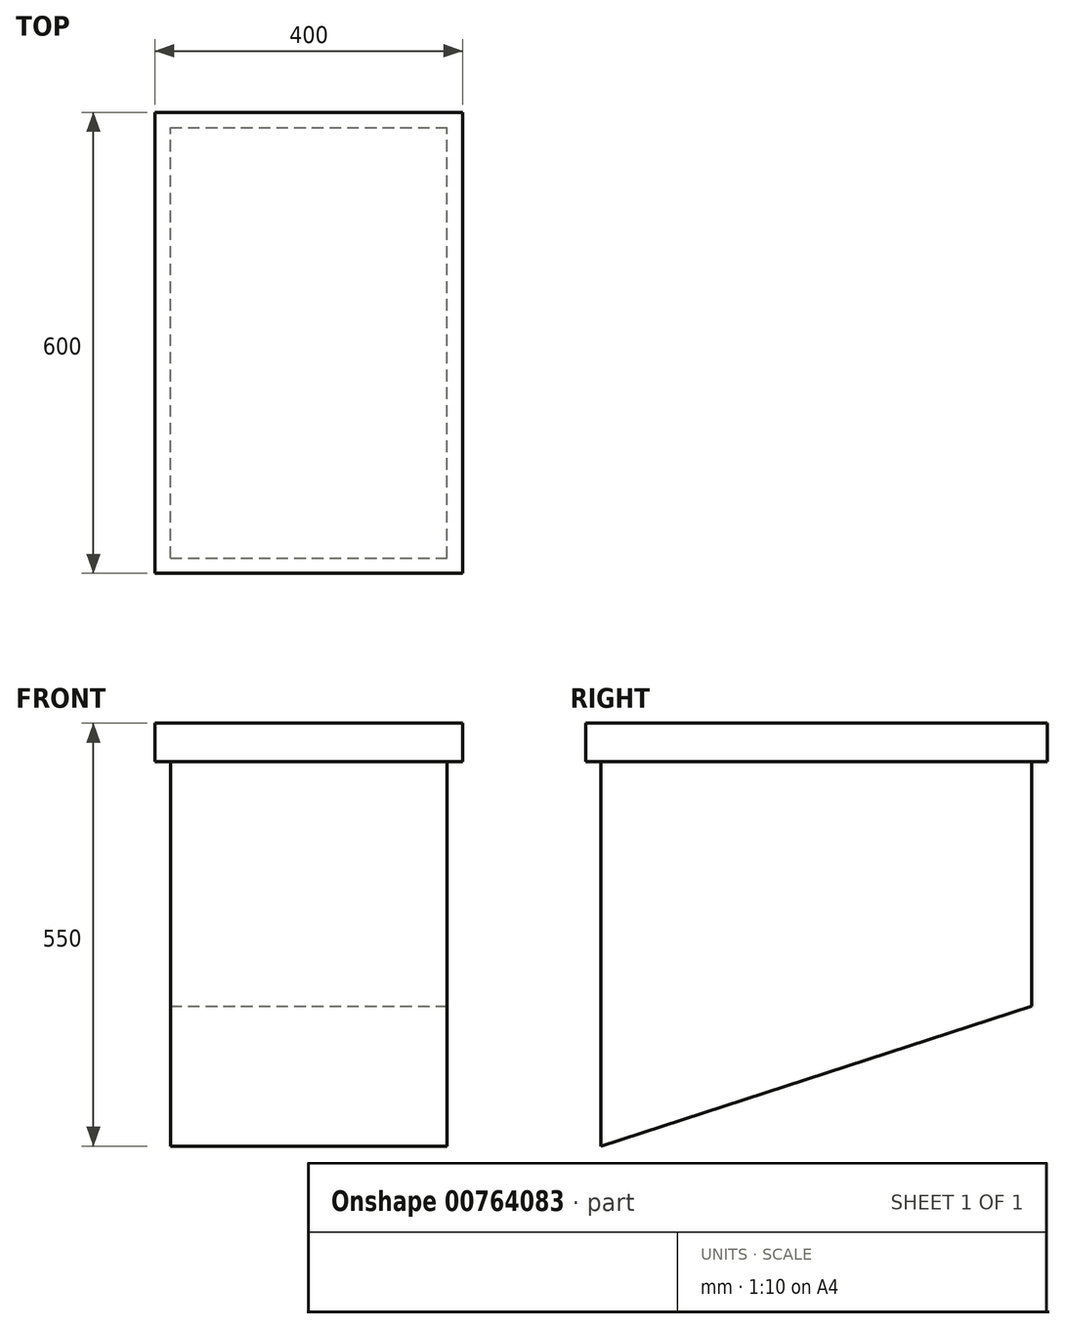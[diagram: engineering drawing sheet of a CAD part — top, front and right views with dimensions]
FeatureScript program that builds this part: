
annotation { "Feature Type Name" : "Feature", "Feature Type Description" : "" }
export const myFeature = defineFeature(function(context is Context, id is Id, definition is map)
    precondition{}
    {
        {
            var Q0;
            Q0=qCreatedBy(makeId("Top.planeOp"),FACE);
            var sketch = newSketch(context, id + "F0", { "sketchPlane" : qUnion([Q0])});
            skLineSegment(sketch, "E0.bottom", {"start": v(-180, 280) * mm, "end": v(180, 280) * mm});
            skLineSegment(sketch, "E0.top", {"start": v(-180, -280) * mm, "end": v(180, -280) * mm});
            skLineSegment(sketch, "E0.left", {"start": v(-180, 280) * mm, "end": v(-180, -280) * mm});
            skLineSegment(sketch, "E0.right", {"start": v(180, 280) * mm, "end": v(180, -280) * mm});
            skPoint(sketch, "E0.middle", {"position": v(0, 0) * mm});
            skSolve(sketch);
        }
        {
            var Q0;
            Q0 = qSketchRegion(id + "F0", true);
            var sketch = newSketch(context, id + "F1", { "sketchPlane" : qUnion([Q0])});
            skSolve(sketch);
        }
        {
            var Q0;
            Q0 = qSketchRegion(id + "F0", true);
            var Q1;
            Q1=makeQuery(id+"F1.imprint","IMPRINT",FACE,{"disambiguationData":[TD([[makeQuery(id+"F1.imprint","IMPRINT",EDGE,{"derivedFrom":makeQuery(id+"F0.imprint","IMPRINT",EDGE,{"derivedFrom":sQuery(id+"F0.wireOp",EDGE,"E0.bottom")})}),-1.0]])]});
            extrude(context, id + "F2", {"entities" : qUnion([Q0, Q1]), "depth" : 500 * mm, "offsetDistance" : 25 * mm});
        }
        {
            var Q0;
            {var subQ0=sQuery(id+"F0.wireOp",EDGE,"E0.right");var subQ1=sQuery(id+"F0.wireOp",EDGE,"E0.left");var subQ2=sQuery(id+"F0.wireOp",EDGE,"E0.top");var subQ3=sQuery(id+"F0.wireOp",EDGE,"E0.bottom");Q0=makeQuery(id+"F2.opExtrude","CAP_FACE",FACE,{"disambiguationData":[OSD([subQ3,subQ2,subQ1,subQ0]),TDD([makeQuery(id+"F0.imprint","IMPRINT",EDGE,{"derivedFrom":subQ3}),makeQuery(id+"F0.imprint","IMPRINT",EDGE,{"derivedFrom":subQ2}),makeQuery(id+"F0.imprint","IMPRINT",EDGE,{"derivedFrom":subQ1}),makeQuery(id+"F0.imprint","IMPRINT",EDGE,{"derivedFrom":subQ0})])],"isStart":false});}
            var sketch = newSketch(context, id + "F3", { "sketchPlane" : qUnion([Q0])});
            skLineSegment(sketch, "E1.bottom", {"start": v(-200, -300) * mm, "end": v(200, -300) * mm});
            skLineSegment(sketch, "E1.top", {"start": v(-200, 300) * mm, "end": v(200, 300) * mm});
            skLineSegment(sketch, "E1.left", {"start": v(-200, -300) * mm, "end": v(-200, 300) * mm});
            skLineSegment(sketch, "E1.right", {"start": v(200, -300) * mm, "end": v(200, 300) * mm});
            skPoint(sketch, "E1.middle", {"position": v(0, 0) * mm});
            skSolve(sketch);
        }
        {
            var Q0;
            Q0 = qSketchRegion(id + "F3", true);
            extrude(context, id + "F4", {"entities" : qUnion([Q0]), "depth" : 50 * mm, "offsetDistance" : 25 * mm});
        }
        {
            var Q0;
            {var subQ0=sQuery(id+"F0.wireOp",EDGE,"E0.right");Q0=makeQuery(id+"F2.opExtrude","SWEPT_FACE",FACE,{"disambiguationData":[OSD([subQ0]),TDD([makeQuery(id+"F1.imprint","IMPRINT",EDGE,{"derivedFrom":makeQuery(id+"F0.imprint","IMPRINT",EDGE,{"derivedFrom":subQ0})})])]});}
            var sketch = newSketch(context, id + "F5", { "sketchPlane" : qUnion([Q0])});
            skLineSegment(sketch, "E2", {"start": v(-280, 0) * mm, "end": v(280, 181.96) * mm});
            skLineSegment(sketch, "E3", {"start": v(-280, 0) * mm, "end": v(280, 0) * mm});
            skLineSegment(sketch, "E4", {"start": v(280, 0) * mm, "end": v(280, 181.96) * mm});
            skSolve(sketch);
        }
        {
            var Q0;
            Q0 = qSketchRegion(id + "F5", true);
            extrude(context, id + "F6", {"entities" : qUnion([Q0]), "operationType" : NewBodyOperationType.REMOVE, "oppositeDirection" : true, "depth" : 800 * mm, "offsetDistance" : 25 * mm});
        }
    });
